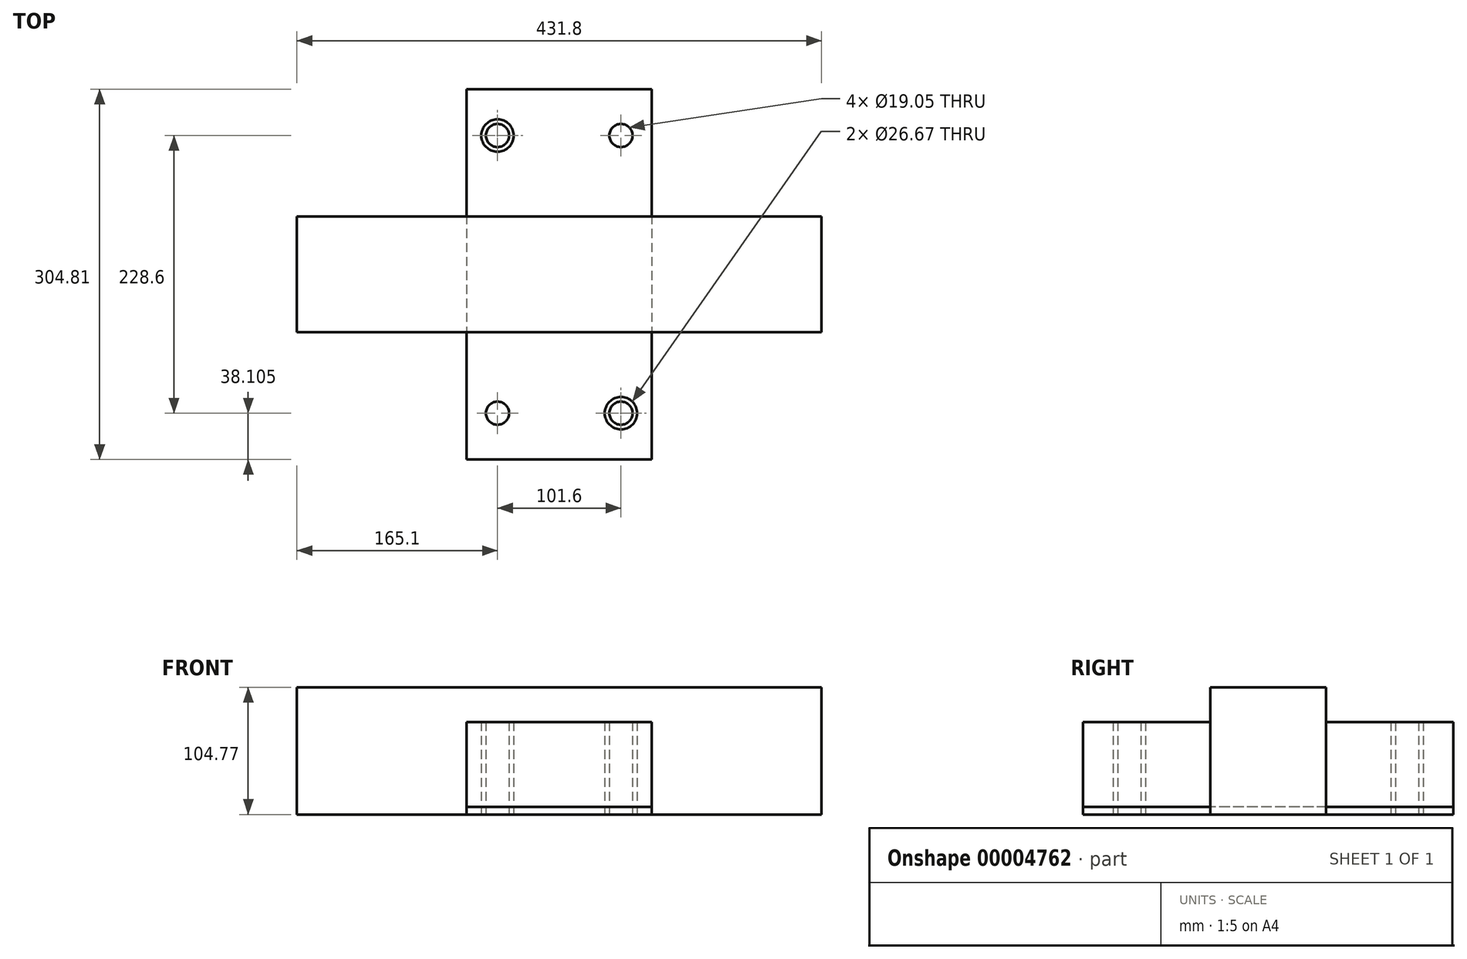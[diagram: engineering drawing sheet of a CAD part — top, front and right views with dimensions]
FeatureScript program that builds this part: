
annotation { "Feature Type Name" : "Feature", "Feature Type Description" : "" }
export const myFeature = defineFeature(function(context is Context, id is Id, definition is map)
    precondition{}
    {
        {
            var Q0;
            Q0=qCreatedBy(makeId("Top.planeOp"),FACE);
            var sketch = newSketch(context, id + "F0", { "sketchPlane" : qUnion([Q0])});
            skLineSegment(sketch, "E0.bottom", {"start": v(0, 0) * mm, "end": v(431.8, 0) * mm});
            skLineSegment(sketch, "E0.top", {"start": v(0, -95.25) * mm, "end": v(431.8, -95.25) * mm});
            skLineSegment(sketch, "E0.left", {"start": v(0, 0) * mm, "end": v(0, -95.25) * mm});
            skLineSegment(sketch, "E0.right", {"start": v(431.8, 0) * mm, "end": v(431.8, -95.25) * mm});
            skLineSegment(sketch, "E1.bottom", {"start": v(139.7, 104.78) * mm, "end": v(292.1, 104.78) * mm});
            skLineSegment(sketch, "E1.top", {"start": v(139.7, -200.02) * mm, "end": v(292.1, -200.02) * mm});
            skLineSegment(sketch, "E1.left", {"start": v(139.7, 104.78) * mm, "end": v(139.7, -200.02) * mm});
            skLineSegment(sketch, "E1.right", {"start": v(292.1, 104.78) * mm, "end": v(292.1, -200.02) * mm});
            skCircle(sketch, "E2", {"center": v(165.1, -161.92) * mm, "radius": 13.34 * mm});
            skCircle(sketch, "E3", {"center": v(165.1, -161.92) * mm, "radius": 9.53 * mm});
            skLineSegment(sketch, "E4", {"start": v(215.9, -200.02) * mm, "end": v(215.9, 104.78) * mm, "construction": true});
            skLineSegment(sketch, "E5", {"start": v(0, -47.63) * mm, "end": v(431.8, -47.62) * mm, "construction": true});
            skCircle(sketch, "E6.MirrorC", {"center": v(266.7, -161.92) * mm, "radius": 13.34 * mm});
            skCircle(sketch, "E7.MirrorC", {"center": v(266.7, -161.92) * mm, "radius": 9.53 * mm});
            skCircle(sketch, "E8.MirrorC", {"center": v(165.1, 66.67) * mm, "radius": 13.34 * mm});
            skCircle(sketch, "E9.MirrorC", {"center": v(165.1, 66.67) * mm, "radius": 9.53 * mm});
            skCircle(sketch, "E10.MirrorC", {"center": v(266.7, 66.67) * mm, "radius": 13.34 * mm});
            skCircle(sketch, "E11.MirrorC", {"center": v(266.7, 66.67) * mm, "radius": 9.53 * mm});
            skSolve(sketch);
        }
        {
            var Q0;
            Q0=makeQuery(id+"F0.imprint","IMPRINT",FACE,{"disambiguationData":[TD([[makeQuery(id+"F0.imprint","IMPRINT",EDGE,{"derivedFrom":sQuery(id+"F0.wireOp",EDGE,"E0.bottom")}),-1.0]])]});
            extrude(context, id + "F1", {"entities" : qUnion([Q0]), "depth" : 104.77 * mm, "offsetDistance" : 25.4 * mm});
        }
        {
            var Q0;
            {var subQ5=sQuery(id+"F0.wireOp",EDGE,"E1.top");Q0=makeQuery(id+"F0.imprint","IMPRINT",FACE,{"disambiguationData":[TD([[makeQuery(id+"F0.imprint","IMPRINT",EDGE,{"derivedFrom":subQ5}),1.0]])]});}
            var Q1;
            {var subQ0=sQuery(id+"F0.wireOp",EDGE,"E1.left");var subQ1=sQuery(id+"F0.wireOp",EDGE,"E0.bottom");var subQ2=makeQuery(id+"F0.imprint","INTERSECT",VERTEX,{"derivedFrom":[subQ1,subQ0]});Q1=makeQuery(id+"F0.imprint","IMPRINT",FACE,{"disambiguationData":[TD([[makeQuery(id+"F0.imprint","IMPRINT",EDGE,{"disambiguationData":[TD([[subQ2,-1.0]])],"derivedFrom":subQ1}),-1.0]])]});}
            var Q2;
            {var subQ5=sQuery(id+"F0.wireOp",EDGE,"E1.bottom");Q2=makeQuery(id+"F0.imprint","IMPRINT",FACE,{"disambiguationData":[TD([[makeQuery(id+"F0.imprint","IMPRINT",EDGE,{"derivedFrom":subQ5}),-1.0]])]});}
            var Q3;
            Q3=makeQuery(id+"F0.imprint","IMPRINT",FACE,{"disambiguationData":[TD([[makeQuery(id+"F0.imprint","IMPRINT",EDGE,{"derivedFrom":sQuery(id+"F0.wireOp",EDGE,"E2")}),1.0]])]});
            var Q4;
            Q4=makeQuery(id+"F0.imprint","IMPRINT",FACE,{"disambiguationData":[TD([[makeQuery(id+"F0.imprint","IMPRINT",EDGE,{"derivedFrom":sQuery(id+"F0.wireOp",EDGE,"E3")}),1.0]])]});
            var Q5;
            Q5=makeQuery(id+"F0.imprint","IMPRINT",FACE,{"disambiguationData":[TD([[makeQuery(id+"F0.imprint","IMPRINT",EDGE,{"derivedFrom":sQuery(id+"F0.wireOp",EDGE,"E6.MirrorC")}),-1.0]])]});
            var Q6;
            Q6=makeQuery(id+"F0.imprint","IMPRINT",FACE,{"disambiguationData":[TD([[makeQuery(id+"F0.imprint","IMPRINT",EDGE,{"derivedFrom":sQuery(id+"F0.wireOp",EDGE,"E7.MirrorC")}),-1.0]])]});
            var Q7;
            Q7=makeQuery(id+"F0.imprint","IMPRINT",FACE,{"disambiguationData":[TD([[makeQuery(id+"F0.imprint","IMPRINT",EDGE,{"derivedFrom":sQuery(id+"F0.wireOp",EDGE,"E10.MirrorC")}),1.0]])]});
            var Q8;
            Q8=makeQuery(id+"F0.imprint","IMPRINT",FACE,{"disambiguationData":[TD([[makeQuery(id+"F0.imprint","IMPRINT",EDGE,{"derivedFrom":sQuery(id+"F0.wireOp",EDGE,"E11.MirrorC")}),1.0]])]});
            var Q9;
            Q9=makeQuery(id+"F0.imprint","IMPRINT",FACE,{"disambiguationData":[TD([[makeQuery(id+"F0.imprint","IMPRINT",EDGE,{"derivedFrom":sQuery(id+"F0.wireOp",EDGE,"E8.MirrorC")}),-1.0]])]});
            var Q10;
            Q10=makeQuery(id+"F0.imprint","IMPRINT",FACE,{"disambiguationData":[TD([[makeQuery(id+"F0.imprint","IMPRINT",EDGE,{"derivedFrom":sQuery(id+"F0.wireOp",EDGE,"E9.MirrorC")}),-1.0]])]});
            extrude(context, id + "F2", {"entities" : qUnion([Q0, Q1, Q2, Q3, Q4, Q5, Q6, Q7, Q8, Q9, Q10]), "depth" : 6.35 * mm, "offsetDistance" : 25.4 * mm});
        }
        {
            var Q0;
            Q0=makeQuery(id+"F0.imprint","IMPRINT",FACE,{"disambiguationData":[TD([[makeQuery(id+"F0.imprint","IMPRINT",EDGE,{"derivedFrom":sQuery(id+"F0.wireOp",EDGE,"E8.MirrorC")}),-1.0]])]});
            var Q1;
            Q1=makeQuery(id+"F0.imprint","IMPRINT",FACE,{"disambiguationData":[TD([[makeQuery(id+"F0.imprint","IMPRINT",EDGE,{"derivedFrom":sQuery(id+"F0.wireOp",EDGE,"E10.MirrorC")}),1.0]])]});
            var Q2;
            Q2=makeQuery(id+"F0.imprint","IMPRINT",FACE,{"disambiguationData":[TD([[makeQuery(id+"F0.imprint","IMPRINT",EDGE,{"derivedFrom":sQuery(id+"F0.wireOp",EDGE,"E6.MirrorC")}),-1.0]])]});
            var Q3;
            Q3=makeQuery(id+"F0.imprint","IMPRINT",FACE,{"disambiguationData":[TD([[makeQuery(id+"F0.imprint","IMPRINT",EDGE,{"derivedFrom":sQuery(id+"F0.wireOp",EDGE,"E2")}),1.0]])]});
            extrude(context, id + "F3", {"entities" : qUnion([Q0, Q1, Q2, Q3]), "depth" : 76.2 * mm, "offsetDistance" : 25.4 * mm});
        }
    });
